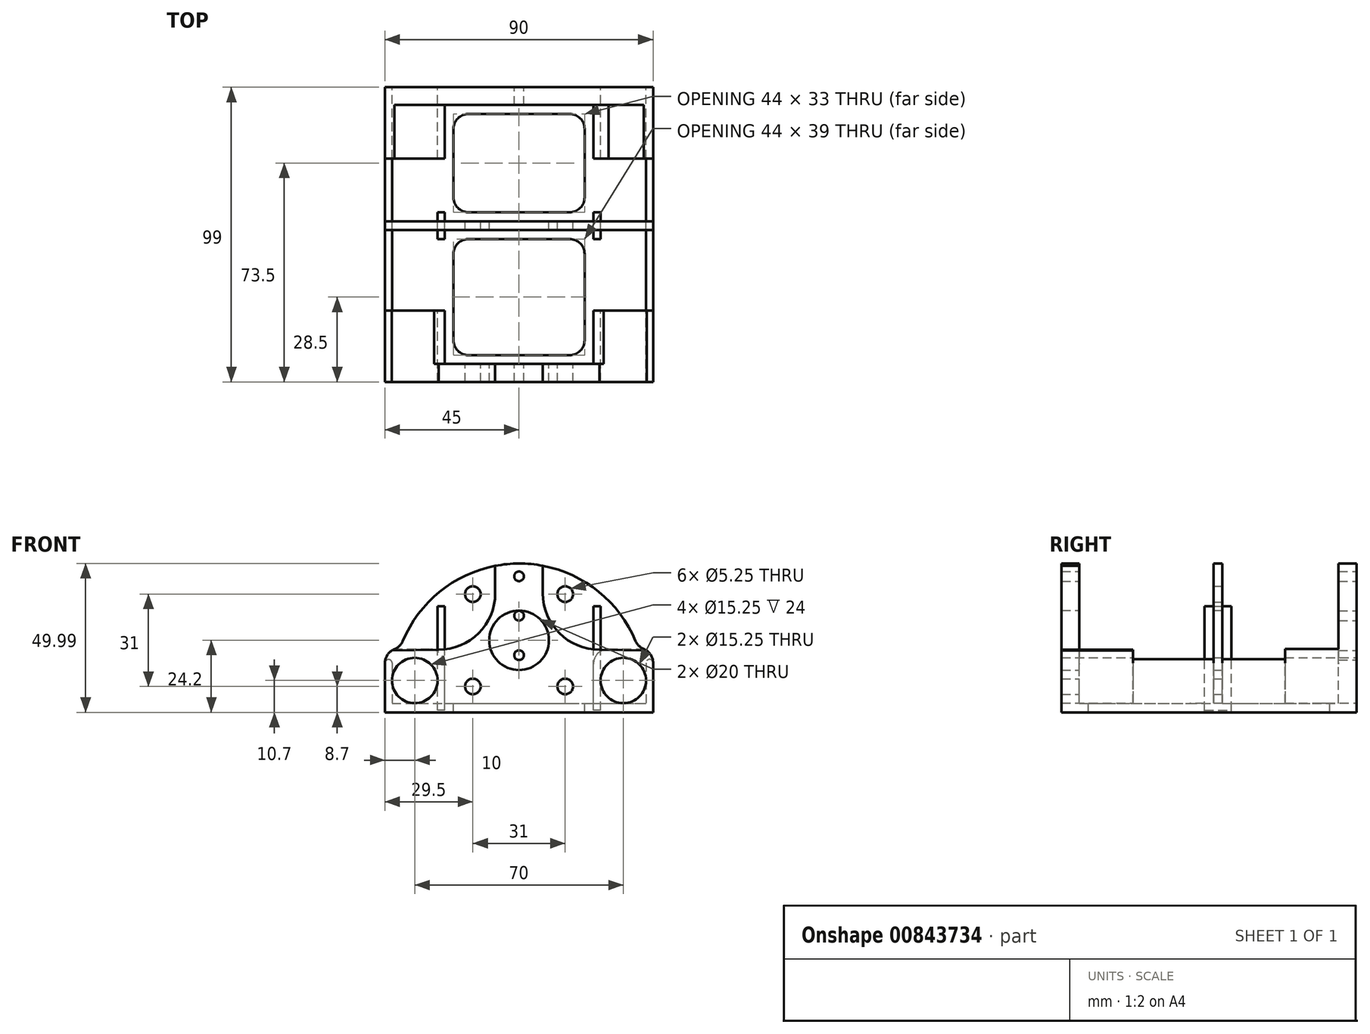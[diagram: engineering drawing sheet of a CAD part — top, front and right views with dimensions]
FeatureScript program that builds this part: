
annotation { "Feature Type Name" : "Feature", "Feature Type Description" : "" }
export const myFeature = defineFeature(function(context is Context, id is Id, definition is map)
    precondition{}
    {
        {
            var Q0;
            Q0=qCreatedBy(makeId("Front.planeOp"),FACE);
            var sketch = newSketch(context, id + "F0", { "sketchPlane" : qUnion([Q0])});
            skLineSegment(sketch, "E0", {"start": v(0, 0) * mm, "end": v(-52.92, 0) * mm, "construction": true});
            skLineSegment(sketch, "E1", {"start": v(-0.02, 0) * mm, "end": v(0, 0) * mm, "construction": true});
            skLineSegment(sketch, "E2", {"start": v(0, 0) * mm, "end": v(0, 49.26) * mm, "construction": true});
            skCircle(sketch, "E3", {"center": v(-35, 0) * mm, "radius": 7.62 * mm});
            skCircle(sketch, "E4", {"center": v(0, 8.5) * mm, "radius": 1.63 * mm});
            skCircle(sketch, "E5", {"center": v(0, 21.75) * mm, "radius": 1.63 * mm});
            skCircle(sketch, "E6", {"center": v(0, 35) * mm, "radius": 1.63 * mm});
            skLineSegment(sketch, "E7", {"start": v(45, 5.93) * mm, "end": v(45, -10) * mm});
            skLineSegment(sketch, "E8", {"start": v(45, -10) * mm, "end": v(-45, -10) * mm});
            skLineSegment(sketch, "E9", {"start": v(-45, -10) * mm, "end": v(-45, 5.86) * mm});
            skLineSegment(sketch, "E10", {"start": v(0, 0) * mm, "end": v(0, -24.97) * mm, "construction": true});
            skCircle(sketch, "E11", {"center": v(15.5, 29) * mm, "radius": 2.62 * mm});
            skCircle(sketch, "E12", {"center": v(-15.5, 29) * mm, "radius": 2.62 * mm});
            skCircle(sketch, "E13", {"center": v(15.5, -2) * mm, "radius": 2.62 * mm});
            skCircle(sketch, "E14", {"center": v(-15.5, -2) * mm, "radius": 2.62 * mm});
            skCircle(sketch, "E15", {"center": v(0, 13.5) * mm, "radius": 10 * mm});
            skLineSegment(sketch, "E16", {"start": v(25, 5.57) * mm, "end": v(25, -10) * mm});
            skLineSegment(sketch, "E17", {"start": v(-25, 5.52) * mm, "end": v(-25, -10) * mm});
            skCircle(sketch, "E18", {"center": v(35, 0) * mm, "radius": 7.62 * mm});
            skLineSegment(sketch, "E19", {"start": v(0, 0) * mm, "end": v(70, 0) * mm, "construction": true});
            skPoint(sketch, "E20.visualSharp", {"position": v(-45, 10) * mm});
            skArc(sketch, "E20.filletArc", {"start": v(-41.8, 10.52) * mm, "mid": v(-44.13, 8.68) * mm, "end": v(-45, 5.86) * mm});
            skArc(sketch, "E21.filletArc", {"start": v(-25, 5.52) * mm, "mid": v(-26.46, 9.06) * mm, "end": v(-30, 10.52) * mm});
            skArc(sketch, "E22.filletArc", {"start": v(30.06, 10.56) * mm, "mid": v(26.49, 9.12) * mm, "end": v(25, 5.57) * mm});
            skPoint(sketch, "E23.visualSharp", {"position": v(45, 10) * mm});
            skArc(sketch, "E23.filletArc", {"start": v(45, 5.93) * mm, "mid": v(44.14, 8.73) * mm, "end": v(41.87, 10.56) * mm});
            skLineSegment(sketch, "E24", {"start": v(42.62, -10) * mm, "end": v(42.62, 5.93) * mm});
            skArc(sketch, "E25", {"start": v(45, 5.93) * mm, "mid": v(43.81, 7.12) * mm, "end": v(42.62, 5.93) * mm});
            skLineSegment(sketch, "E26", {"start": v(-42.62, -10) * mm, "end": v(-42.62, 5.86) * mm});
            skArc(sketch, "E27", {"start": v(-42.62, 5.86) * mm, "mid": v(-43.81, 7.05) * mm, "end": v(-45, 5.86) * mm});
            skArc(sketch, "E28", {"start": v(39.13, 13.27) * mm, "mid": v(0.06, 39.29) * mm, "end": v(-39, 13.26) * mm});
            skPoint(sketch, "E29.visualSharp", {"position": v(-39.92, 10.86) * mm});
            skArc(sketch, "E29.filletArc", {"start": v(-41.8, 10.52) * mm, "mid": v(-40.13, 11.6) * mm, "end": v(-39, 13.26) * mm});
            skPoint(sketch, "E30.visualSharp", {"position": v(40.03, 10.93) * mm});
            skArc(sketch, "E30.filletArc", {"start": v(39.13, 13.27) * mm, "mid": v(40.23, 11.64) * mm, "end": v(41.87, 10.56) * mm});
            skLineSegment(sketch, "E31", {"start": v(-41.8, 10.52) * mm, "end": v(-30, 10.52) * mm});
            skLineSegment(sketch, "E32", {"start": v(41.87, 10.56) * mm, "end": v(30.06, 10.56) * mm});
            skLineSegment(sketch, "E33", {"start": v(22.5, -10) * mm, "end": v(22.5, 0) * mm});
            skLineSegment(sketch, "E34", {"start": v(27.38, -10) * mm, "end": v(27.38, 25) * mm});
            skLineSegment(sketch, "E35", {"start": v(25, 5.57) * mm, "end": v(25, 25) * mm});
            skLineSegment(sketch, "E36", {"start": v(25, 25) * mm, "end": v(27.38, 25) * mm});
            skLineSegment(sketch, "E37", {"start": v(-27.38, -10) * mm, "end": v(-27.38, 25) * mm});
            skLineSegment(sketch, "E38", {"start": v(-25, 5.52) * mm, "end": v(-25, 25) * mm});
            skLineSegment(sketch, "E39", {"start": v(-25, 25) * mm, "end": v(-27.38, 25) * mm});
            skSolve(sketch);
        }
        {
            var Q0;
            Q0=makeQuery(id+"F0.imprint","IMPRINT",FACE,{"disambiguationData":[TD([[makeQuery(id+"F0.imprint","IMPRINT",EDGE,{"derivedFrom":sQuery(id+"F0.wireOp",EDGE,"E6")}),-1.0]])]});
            var Q1;
            {var subQ4=sQuery(id+"F0.wireOp",EDGE,"E7");Q1=makeQuery(id+"F0.imprint","IMPRINT",FACE,{"disambiguationData":[TD([[makeQuery(id+"F0.imprint","IMPRINT",EDGE,{"derivedFrom":subQ4}),-1.0]])]});}
            var Q2;
            {var subQ6=sQuery(id+"F0.wireOp",EDGE,"ls8kvNI4-NHHg-Onv5-wAsb-4FJF5Vd8KV6a");Q2=makeQuery(id+"F0.imprint","IMPRINT",FACE,{"disambiguationData":[TD([[makeQuery(id+"F0.imprint","IMPRINT",EDGE,{"derivedFrom":subQ6}),-1.0]])]});}
            var Q3;
            {var subQ0=sQuery(id+"F0.wireOp",EDGE,"E17");Q3=makeQuery(id+"F0.imprint","IMPRINT",FACE,{"disambiguationData":[TD([[makeQuery(id+"F0.imprint","IMPRINT",EDGE,{"derivedFrom":subQ0}),-1.0]])]});}
            var Q4;
            {var subQ1=sQuery(id+"F0.wireOp",EDGE,"E9");Q4=makeQuery(id+"F0.imprint","IMPRINT",FACE,{"disambiguationData":[TD([[makeQuery(id+"F0.imprint","IMPRINT",EDGE,{"derivedFrom":subQ1}),-1.0]])]});}
            var Q5;
            Q5=makeQuery(id+"F0.imprint","IMPRINT",FACE,{"disambiguationData":[TD([[makeQuery(id+"F0.imprint","IMPRINT",EDGE,{"derivedFrom":sQuery(id+"F0.wireOp",EDGE,"E11")}),1.0]])]});
            var Q6;
            Q6=makeQuery(id+"F0.imprint","IMPRINT",FACE,{"disambiguationData":[TD([[makeQuery(id+"F0.imprint","IMPRINT",EDGE,{"derivedFrom":sQuery(id+"F0.wireOp",EDGE,"E12")}),1.0]])]});
            var Q7;
            Q7=makeQuery(id+"F0.imprint","IMPRINT",FACE,{"disambiguationData":[TD([[makeQuery(id+"F0.imprint","IMPRINT",EDGE,{"derivedFrom":sQuery(id+"F0.wireOp",EDGE,"E4")}),-1.0]])]});
            var Q8;
            Q8=makeQuery(id+"F0.imprint","IMPRINT",FACE,{"disambiguationData":[TD([[makeQuery(id+"F0.imprint","IMPRINT",EDGE,{"derivedFrom":sQuery(id+"F0.wireOp",EDGE,"E14")}),1.0]])]});
            var Q9;
            Q9=makeQuery(id+"F0.imprint","IMPRINT",FACE,{"disambiguationData":[TD([[makeQuery(id+"F0.imprint","IMPRINT",EDGE,{"derivedFrom":sQuery(id+"F0.wireOp",EDGE,"E13")}),1.0]])]});
            var Q10;
            {var subQ0=sQuery(id+"F0.wireOp",EDGE,"E16");Q10=makeQuery(id+"F0.imprint","IMPRINT",FACE,{"disambiguationData":[TD([[makeQuery(id+"F0.imprint","IMPRINT",EDGE,{"derivedFrom":subQ0}),1.0]])]});}
            var Q11;
            {var subQ1=sQuery(id+"F0.wireOp",EDGE,"E16");Q11=makeQuery(id+"F0.imprint","IMPRINT",FACE,{"disambiguationData":[TD([[makeQuery(id+"F0.imprint","IMPRINT",EDGE,{"derivedFrom":subQ1}),-1.0]])]});}
            var Q12;
            {var subQ1=sQuery(id+"F0.wireOp",EDGE,"E17");Q12=makeQuery(id+"F0.imprint","IMPRINT",FACE,{"disambiguationData":[TD([[makeQuery(id+"F0.imprint","IMPRINT",EDGE,{"derivedFrom":subQ1}),1.0]])]});}
            var Q13;
            {var subQ0=sQuery(id+"F0.wireOp",EDGE,"E35");Q13=makeQuery(id+"F0.imprint","IMPRINT",FACE,{"disambiguationData":[TD([[makeQuery(id+"F0.imprint","IMPRINT",EDGE,{"derivedFrom":subQ0}),-1.0]])]});}
            var Q14;
            {var subQ0=sQuery(id+"F0.wireOp",EDGE,"E38");Q14=makeQuery(id+"F0.imprint","IMPRINT",FACE,{"disambiguationData":[TD([[makeQuery(id+"F0.imprint","IMPRINT",EDGE,{"derivedFrom":subQ0}),1.0]])]});}
            var Q15;
            Q15=makeQuery(id+"F0.imprint","IMPRINT",FACE,{"disambiguationData":[TD([[makeQuery(id+"F0.imprint","IMPRINT",EDGE,{"derivedFrom":sQuery(id+"F0.wireOp",EDGE,"E23.filletArc")}),1.0]])]});
            var Q16;
            Q16=makeQuery(id+"F0.imprint","IMPRINT",FACE,{"disambiguationData":[TD([[makeQuery(id+"F0.imprint","IMPRINT",EDGE,{"derivedFrom":sQuery(id+"F0.wireOp",EDGE,"E20.filletArc")}),1.0]])]});
            var Q17;
            {var subQ0=sQuery(id+"F0.wireOp",EDGE,"E26");var subQ1=sQuery(id+"F0.wireOp",EDGE,"E3");var subQ2=makeQuery(id+"F0.imprint","INTERSECT",VERTEX,{"derivedFrom":[subQ1,subQ0]});Q17=makeQuery(id+"F0.imprint","IMPRINT",FACE,{"disambiguationData":[TD([[makeQuery(id+"F0.imprint","IMPRINT",EDGE,{"disambiguationData":[TD([[subQ2,-1.0]])],"derivedFrom":subQ1}),-1.0]])]});}
            var Q18;
            {var subQ0=sQuery(id+"F0.wireOp",EDGE,"E24");var subQ1=sQuery(id+"F0.wireOp",EDGE,"E8");var subQ2=makeQuery(id+"F0.imprint","INTERSECT",VERTEX,{"derivedFrom":[subQ1,subQ0]});Q18=makeQuery(id+"F0.imprint","IMPRINT",FACE,{"disambiguationData":[TD([[makeQuery(id+"F0.imprint","IMPRINT",EDGE,{"disambiguationData":[TD([[subQ2,-1.0]])],"derivedFrom":subQ1}),-1.0]])]});}
            extrude(context, id + "F1", {"entities" : qUnion([Q0, Q1, Q2, Q3, Q4, Q5, Q6, Q7, Q8, Q9, Q10, Q11, Q12, Q13, Q14, Q15, Q16, Q17, Q18]), "depth" : 6 * mm, "offsetDistance" : 25 * mm});
        }
        {
            var Q0;
            Q0=makeQuery(id+"F0.imprint","IMPRINT",FACE,{"disambiguationData":[TD([[makeQuery(id+"F0.imprint","IMPRINT",EDGE,{"derivedFrom":sQuery(id+"F0.wireOp",EDGE,"E6")}),-1.0]])]});
            var Q1;
            {var subQ0=sQuery(id+"F0.wireOp",EDGE,"E16");Q1=makeQuery(id+"F0.imprint","IMPRINT",FACE,{"disambiguationData":[TD([[makeQuery(id+"F0.imprint","IMPRINT",EDGE,{"derivedFrom":subQ0}),1.0]])]});}
            var Q2;
            {var subQ4=sQuery(id+"F0.wireOp",EDGE,"E7");Q2=makeQuery(id+"F0.imprint","IMPRINT",FACE,{"disambiguationData":[TD([[makeQuery(id+"F0.imprint","IMPRINT",EDGE,{"derivedFrom":subQ4}),-1.0]])]});}
            var Q3;
            {var subQ4=sQuery(id+"F0.wireOp",EDGE,"E9");Q3=makeQuery(id+"F0.imprint","IMPRINT",FACE,{"disambiguationData":[TD([[makeQuery(id+"F0.imprint","IMPRINT",EDGE,{"derivedFrom":subQ4}),-1.0]])]});}
            var Q4;
            Q4=makeQuery(id+"F0.imprint","IMPRINT",FACE,{"disambiguationData":[TD([[makeQuery(id+"F0.imprint","IMPRINT",EDGE,{"derivedFrom":sQuery(id+"F0.wireOp",EDGE,"E6")}),1.0]])]});
            var Q5;
            {var subQ1=sQuery(id+"F0.wireOp",EDGE,"E16");Q5=makeQuery(id+"F0.imprint","IMPRINT",FACE,{"disambiguationData":[TD([[makeQuery(id+"F0.imprint","IMPRINT",EDGE,{"derivedFrom":subQ1}),-1.0]])]});}
            var Q6;
            {var subQ1=sQuery(id+"F0.wireOp",EDGE,"E17");Q6=makeQuery(id+"F0.imprint","IMPRINT",FACE,{"disambiguationData":[TD([[makeQuery(id+"F0.imprint","IMPRINT",EDGE,{"derivedFrom":subQ1}),1.0]])]});}
            var Q7;
            Q7=makeQuery(id+"F0.imprint","IMPRINT",FACE,{"disambiguationData":[TD([[makeQuery(id+"F0.imprint","IMPRINT",EDGE,{"derivedFrom":sQuery(id+"F0.wireOp",EDGE,"E23.filletArc")}),1.0]])]});
            var Q8;
            {var subQ0=sQuery(id+"F0.wireOp",EDGE,"E24");var subQ1=sQuery(id+"F0.wireOp",EDGE,"E8");var subQ2=makeQuery(id+"F0.imprint","INTERSECT",VERTEX,{"derivedFrom":[subQ1,subQ0]});Q8=makeQuery(id+"F0.imprint","IMPRINT",FACE,{"disambiguationData":[TD([[makeQuery(id+"F0.imprint","IMPRINT",EDGE,{"disambiguationData":[TD([[subQ2,-1.0]])],"derivedFrom":subQ1}),-1.0]])]});}
            var Q9;
            Q9=makeQuery(id+"F0.imprint","IMPRINT",FACE,{"disambiguationData":[TD([[makeQuery(id+"F0.imprint","IMPRINT",EDGE,{"derivedFrom":sQuery(id+"F0.wireOp",EDGE,"E20.filletArc")}),1.0]])]});
            var Q10;
            {var subQ0=sQuery(id+"F0.wireOp",EDGE,"E35");Q10=makeQuery(id+"F0.imprint","IMPRINT",FACE,{"disambiguationData":[TD([[makeQuery(id+"F0.imprint","IMPRINT",EDGE,{"derivedFrom":subQ0}),-1.0]])]});}
            var Q11;
            {var subQ0=sQuery(id+"F0.wireOp",EDGE,"E38");Q11=makeQuery(id+"F0.imprint","IMPRINT",FACE,{"disambiguationData":[TD([[makeQuery(id+"F0.imprint","IMPRINT",EDGE,{"derivedFrom":subQ0}),1.0]])]});}
            var Q12;
            {var subQ1=sQuery(id+"F0.wireOp",EDGE,"E17");Q12=makeQuery(id+"F0.imprint","IMPRINT",FACE,{"disambiguationData":[TD([[makeQuery(id+"F0.imprint","IMPRINT",EDGE,{"derivedFrom":subQ1}),-1.0]])]});}
            var Q13;
            {var subQ0=sQuery(id+"F0.wireOp",EDGE,"E26");var subQ1=sQuery(id+"F0.wireOp",EDGE,"E3");var subQ2=makeQuery(id+"F0.imprint","INTERSECT",VERTEX,{"derivedFrom":[subQ1,subQ0]});Q13=makeQuery(id+"F0.imprint","IMPRINT",FACE,{"disambiguationData":[TD([[makeQuery(id+"F0.imprint","IMPRINT",EDGE,{"disambiguationData":[TD([[subQ2,-1.0]])],"derivedFrom":subQ1}),-1.0]])]});}
            extrude(context, id + "F2", {"entities" : qUnion([Q0, Q1, Q2, Q3, Q4, Q5, Q6, Q7, Q8, Q9, Q10, Q11, Q12, Q13]), "depth" : 48 * mm, "offsetDistance" : 25 * mm, "hasSecondDirection" : true, "secondDirectionOppositeDirection" : false, "secondDirectionDepth" : 45 * mm});
        }
        {
            var Q0;
            Q0 = qSketchRegion(id + "F0", true);
            var Q1;
            {var subQ0=sQuery(id+"F0.wireOp",EDGE,"E35");Q1=makeQuery(id+"F0.imprint","IMPRINT",FACE,{"disambiguationData":[TD([[makeQuery(id+"F0.imprint","IMPRINT",EDGE,{"derivedFrom":subQ0}),-1.0]])]});}
            var Q2;
            {var subQ0=sQuery(id+"F0.wireOp",EDGE,"E38");Q2=makeQuery(id+"F0.imprint","IMPRINT",FACE,{"disambiguationData":[TD([[makeQuery(id+"F0.imprint","IMPRINT",EDGE,{"derivedFrom":subQ0}),1.0]])]});}
            extrude(context, id + "F3", {"entities" : qUnion([Q0, Q1, Q2]), "depth" : 99 * mm, "offsetDistance" : 25 * mm, "hasSecondDirection" : true, "secondDirectionOppositeDirection" : false, "secondDirectionDepth" : 93 * mm});
        }
        {
            var Q0;
            Q0=makeQuery(id+"F0.imprint","IMPRINT",FACE,{"disambiguationData":[TD([[makeQuery(id+"F0.imprint","IMPRINT",EDGE,{"derivedFrom":sQuery(id+"F0.wireOp",EDGE,"E23.filletArc")}),1.0]])]});
            var Q1;
            {var subQ4=sQuery(id+"F0.wireOp",EDGE,"E16");Q1=makeQuery(id+"F0.imprint","IMPRINT",FACE,{"disambiguationData":[TD([[makeQuery(id+"F0.imprint","IMPRINT",EDGE,{"derivedFrom":subQ4}),1.0]])]});}
            var Q2;
            {var subQ0=sQuery(id+"F0.wireOp",EDGE,"E24");var subQ1=sQuery(id+"F0.wireOp",EDGE,"E8");var subQ2=makeQuery(id+"F0.imprint","INTERSECT",VERTEX,{"derivedFrom":[subQ1,subQ0]});Q2=makeQuery(id+"F0.imprint","IMPRINT",FACE,{"disambiguationData":[TD([[makeQuery(id+"F0.imprint","IMPRINT",EDGE,{"disambiguationData":[TD([[subQ2,-1.0]])],"derivedFrom":subQ1}),-1.0]])]});}
            var Q3;
            {var subQ4=sQuery(id+"F0.wireOp",EDGE,"E7");Q3=makeQuery(id+"F0.imprint","IMPRINT",FACE,{"disambiguationData":[TD([[makeQuery(id+"F0.imprint","IMPRINT",EDGE,{"derivedFrom":subQ4}),-1.0]])]});}
            var Q4;
            Q4=makeQuery(id+"F0.imprint","IMPRINT",FACE,{"disambiguationData":[TD([[makeQuery(id+"F0.imprint","IMPRINT",EDGE,{"derivedFrom":sQuery(id+"F0.wireOp",EDGE,"E20.filletArc")}),1.0]])]});
            var Q5;
            {var subQ0=sQuery(id+"F0.wireOp",EDGE,"E26");var subQ1=sQuery(id+"F0.wireOp",EDGE,"E3");var subQ2=makeQuery(id+"F0.imprint","INTERSECT",VERTEX,{"derivedFrom":[subQ1,subQ0]});Q5=makeQuery(id+"F0.imprint","IMPRINT",FACE,{"disambiguationData":[TD([[makeQuery(id+"F0.imprint","IMPRINT",EDGE,{"disambiguationData":[TD([[subQ2,-1.0]])],"derivedFrom":subQ1}),-1.0]])]});}
            var Q6;
            {var subQ3=sQuery(id+"F0.wireOp",EDGE,"E9");Q6=makeQuery(id+"F0.imprint","IMPRINT",FACE,{"disambiguationData":[TD([[makeQuery(id+"F0.imprint","IMPRINT",EDGE,{"derivedFrom":subQ3}),-1.0]])]});}
            var Q7;
            {var subQ1=sQuery(id+"F0.wireOp",EDGE,"E17");Q7=makeQuery(id+"F0.imprint","IMPRINT",FACE,{"disambiguationData":[TD([[makeQuery(id+"F0.imprint","IMPRINT",EDGE,{"derivedFrom":subQ1}),-1.0]])]});}
            extrude(context, id + "F4", {"entities" : qUnion([Q0, Q1, Q2, Q3, Q4, Q5, Q6, Q7]), "operationType" : NewBodyOperationType.ADD, "depth" : 24 * mm, "offsetDistance" : 25 * mm});
        }
        {
            var Q0;
            Q0=makeQuery(id+"F0.imprint","IMPRINT",FACE,{"disambiguationData":[TD([[makeQuery(id+"F0.imprint","IMPRINT",EDGE,{"derivedFrom":sQuery(id+"F0.wireOp",EDGE,"ls8kvNI4-NHHg-Onv5-wAsb-4FJF5Vd8KV6a")}),-1.0]])]});
            var Q1;
            {var subQ0=sQuery(id+"F0.wireOp",EDGE,"E16");Q1=makeQuery(id+"F0.imprint","IMPRINT",FACE,{"disambiguationData":[TD([[makeQuery(id+"F0.imprint","IMPRINT",EDGE,{"derivedFrom":subQ0}),1.0]])]});}
            var Q2;
            {var subQ4=sQuery(id+"F0.wireOp",EDGE,"E7");Q2=makeQuery(id+"F0.imprint","IMPRINT",FACE,{"disambiguationData":[TD([[makeQuery(id+"F0.imprint","IMPRINT",EDGE,{"derivedFrom":subQ4}),-1.0]])]});}
            var Q3;
            {var subQ4=sQuery(id+"F0.wireOp",EDGE,"E9");Q3=makeQuery(id+"F0.imprint","IMPRINT",FACE,{"disambiguationData":[TD([[makeQuery(id+"F0.imprint","IMPRINT",EDGE,{"derivedFrom":subQ4}),-1.0]])]});}
            var Q4;
            Q4=makeQuery(id+"F0.imprint","IMPRINT",FACE,{"disambiguationData":[TD([[makeQuery(id+"F0.imprint","IMPRINT",EDGE,{"derivedFrom":sQuery(id+"F0.wireOp",EDGE,"E23.filletArc")}),1.0]])]});
            var Q5;
            {var subQ0=sQuery(id+"F0.wireOp",EDGE,"E24");var subQ1=sQuery(id+"F0.wireOp",EDGE,"E8");var subQ2=makeQuery(id+"F0.imprint","INTERSECT",VERTEX,{"derivedFrom":[subQ1,subQ0]});Q5=makeQuery(id+"F0.imprint","IMPRINT",FACE,{"disambiguationData":[TD([[makeQuery(id+"F0.imprint","IMPRINT",EDGE,{"disambiguationData":[TD([[subQ2,-1.0]])],"derivedFrom":subQ1}),-1.0]])]});}
            var Q6;
            Q6=makeQuery(id+"F0.imprint","IMPRINT",FACE,{"disambiguationData":[TD([[makeQuery(id+"F0.imprint","IMPRINT",EDGE,{"derivedFrom":sQuery(id+"F0.wireOp",EDGE,"E20.filletArc")}),1.0]])]});
            var Q7;
            {var subQ1=sQuery(id+"F0.wireOp",EDGE,"E17");Q7=makeQuery(id+"F0.imprint","IMPRINT",FACE,{"disambiguationData":[TD([[makeQuery(id+"F0.imprint","IMPRINT",EDGE,{"derivedFrom":subQ1}),-1.0]])]});}
            var Q8;
            {var subQ0=sQuery(id+"F0.wireOp",EDGE,"E26");var subQ1=sQuery(id+"F0.wireOp",EDGE,"E3");var subQ2=makeQuery(id+"F0.imprint","INTERSECT",VERTEX,{"derivedFrom":[subQ1,subQ0]});Q8=makeQuery(id+"F0.imprint","IMPRINT",FACE,{"disambiguationData":[TD([[makeQuery(id+"F0.imprint","IMPRINT",EDGE,{"disambiguationData":[TD([[subQ2,-1.0]])],"derivedFrom":subQ1}),-1.0]])]});}
            extrude(context, id + "F5", {"entities" : qUnion([Q0, Q1, Q2, Q3, Q4, Q5, Q6, Q7, Q8]), "operationType" : NewBodyOperationType.ADD, "depth" : 99 * mm, "offsetDistance" : 25 * mm, "hasSecondDirection" : true, "secondDirectionOppositeDirection" : false, "secondDirectionDepth" : 75 * mm});
        }
        {
            var Q0;
            Q0=makeQuery(id+"F0.imprint","IMPRINT",FACE,{"disambiguationData":[TD([[makeQuery(id+"F0.imprint","IMPRINT",EDGE,{"derivedFrom":sQuery(id+"F0.wireOp",EDGE,"E6")}),-1.0]])]});
            var sketch = newSketch(context, id + "F6", { "sketchPlane" : qUnion([Q0])});
            skLineSegment(sketch, "E40.bottom", {"start": v(45, -10.7) * mm, "end": v(-45, -10.7) * mm});
            skLineSegment(sketch, "E40.top", {"start": v(45, -7.7) * mm, "end": v(-45, -7.7) * mm});
            skLineSegment(sketch, "E40.left", {"start": v(45, -10.7) * mm, "end": v(45, -7.7) * mm});
            skLineSegment(sketch, "E40.right", {"start": v(-45, -10.7) * mm, "end": v(-45, -7.7) * mm});
            skLineSegment(sketch, "E41", {"start": v(0, 0) * mm, "end": v(0, -26.9) * mm, "construction": true});
            skSolve(sketch);
        }
        {
            var Q0;
            Q0 = qSketchRegion(id + "F6", true);
            extrude(context, id + "F7", {"entities" : qUnion([Q0]), "depth" : 99 * mm, "offsetDistance" : 25 * mm});
        }
        {
            var Q0;
            Q0=makeQuery(id+"F7.opExtrude","SWEPT_FACE",FACE,{"disambiguationData":[OSD([sQuery(id+"F6.wireOp",EDGE,"E40.top")])]});
            var sketch = newSketch(context, id + "F8", { "sketchPlane" : qUnion([Q0])});
            skLineSegment(sketch, "E42.bottom", {"start": v(-17, -90) * mm, "end": v(17, -90) * mm});
            skLineSegment(sketch, "E42.top", {"start": v(-17, -51) * mm, "end": v(17, -51) * mm});
            skLineSegment(sketch, "E42.left", {"start": v(-22, -85) * mm, "end": v(-22, -56) * mm});
            skLineSegment(sketch, "E42.right", {"start": v(22, -85) * mm, "end": v(22, -56) * mm});
            skLineSegment(sketch, "E43.bottom", {"start": v(-17, -42) * mm, "end": v(17, -42) * mm});
            skLineSegment(sketch, "E43.top", {"start": v(-17, -9) * mm, "end": v(17, -9) * mm});
            skLineSegment(sketch, "E43.left", {"start": v(-22, -37) * mm, "end": v(-22, -14) * mm});
            skLineSegment(sketch, "E43.right", {"start": v(22, -37) * mm, "end": v(22, -14) * mm});
            skLineSegment(sketch, "E44", {"start": v(0, 0) * mm, "end": v(0, -96.08) * mm, "construction": true});
            skPoint(sketch, "E45.visualSharp", {"position": v(22, -9) * mm});
            skArc(sketch, "E45.filletArc", {"start": v(22, -14) * mm, "mid": v(20.54, -10.46) * mm, "end": v(17, -9) * mm});
            skPoint(sketch, "E46.visualSharp", {"position": v(22, -42) * mm});
            skArc(sketch, "E46.filletArc", {"start": v(17, -42) * mm, "mid": v(20.54, -40.54) * mm, "end": v(22, -37) * mm});
            skPoint(sketch, "E47.visualSharp", {"position": v(22, -51) * mm});
            skArc(sketch, "E47.filletArc", {"start": v(22, -56) * mm, "mid": v(20.54, -52.46) * mm, "end": v(17, -51) * mm});
            skPoint(sketch, "E48.visualSharp", {"position": v(22, -90) * mm});
            skArc(sketch, "E48.filletArc", {"start": v(17, -90) * mm, "mid": v(20.54, -88.54) * mm, "end": v(22, -85) * mm});
            skPoint(sketch, "E49.visualSharp", {"position": v(-22, -90) * mm});
            skArc(sketch, "E49.filletArc", {"start": v(-22, -85) * mm, "mid": v(-20.54, -88.54) * mm, "end": v(-17, -90) * mm});
            skPoint(sketch, "E50.visualSharp", {"position": v(-22, -51) * mm});
            skArc(sketch, "E50.filletArc", {"start": v(-17, -51) * mm, "mid": v(-20.54, -52.46) * mm, "end": v(-22, -56) * mm});
            skPoint(sketch, "E51.visualSharp", {"position": v(-22, -42) * mm});
            skArc(sketch, "E51.filletArc", {"start": v(-22, -37) * mm, "mid": v(-20.54, -40.54) * mm, "end": v(-17, -42) * mm});
            skPoint(sketch, "E52.visualSharp", {"position": v(-22, -9) * mm});
            skArc(sketch, "E52.filletArc", {"start": v(-17, -9) * mm, "mid": v(-20.54, -10.46) * mm, "end": v(-22, -14) * mm});
            skSolve(sketch);
        }
        {
            var Q0;
            Q0=makeQuery(id+"F8.imprint","IMPRINT",FACE,{"disambiguationData":[TD([[makeQuery(id+"F8.imprint","IMPRINT",EDGE,{"derivedFrom":sQuery(id+"F8.wireOp",EDGE,"E42.bottom")}),1.0]])]});
            var Q1;
            Q1=makeQuery(id+"F8.imprint","IMPRINT",FACE,{"disambiguationData":[TD([[makeQuery(id+"F8.imprint","IMPRINT",EDGE,{"derivedFrom":sQuery(id+"F8.wireOp",EDGE,"E43.bottom")}),1.0]])]});
            extrude(context, id + "F9", {"entities" : qUnion([Q0, Q1]), "operationType" : NewBodyOperationType.REMOVE, "oppositeDirection" : true, "depth" : 25 * mm, "offsetDistance" : 25 * mm});
        }
        {
            var Q0;
            {var subQ4=sQuery(id+"F0.wireOp",EDGE,"E7");Q0=makeQuery(id+"F0.imprint","IMPRINT",FACE,{"disambiguationData":[TD([[makeQuery(id+"F0.imprint","IMPRINT",EDGE,{"derivedFrom":subQ4}),-1.0]])]});}
            var Q1;
            {var subQ4=sQuery(id+"F0.wireOp",EDGE,"E9");Q1=makeQuery(id+"F0.imprint","IMPRINT",FACE,{"disambiguationData":[TD([[makeQuery(id+"F0.imprint","IMPRINT",EDGE,{"derivedFrom":subQ4}),-1.0]])]});}
            extrude(context, id + "F10", {"entities" : qUnion([Q0, Q1]), "operationType" : NewBodyOperationType.ADD, "depth" : 93 * mm, "offsetDistance" : 25 * mm});
        }
        {
            var Q0;
            Q0=makeQuery(id+"F3.opExtrude","CAP_FACE",FACE,{"disambiguationData":[OSD([sQuery(id+"F0.wireOp",EDGE,"E3"),sQuery(id+"F0.wireOp",EDGE,"E4"),sQuery(id+"F0.wireOp",EDGE,"E5"),sQuery(id+"F0.wireOp",EDGE,"E6"),sQuery(id+"F0.wireOp",EDGE,"E7"),sQuery(id+"F0.wireOp",EDGE,"E8"),sQuery(id+"F0.wireOp",EDGE,"E9"),sQuery(id+"F0.wireOp",EDGE,"xWTqpVJG-LeZE-ckjX-DmdP-jzXZU0kw2qfi"),sQuery(id+"F0.wireOp",EDGE,"E18")])],"isStart":false});
            var sketch = newSketch(context, id + "F11", { "sketchPlane" : qUnion([Q0])});
            skArc(sketch, "E53", {"start": v(-27, 10.32) * mm, "mid": v(-13.56, 15.89) * mm, "end": v(-8, 29.32) * mm});
            skArc(sketch, "E54", {"start": v(8, 29.32) * mm, "mid": v(13.56, 15.89) * mm, "end": v(27, 10.32) * mm});
            skLineSegment(sketch, "E55", {"start": v(-55.07, 10.32) * mm, "end": v(54.12, 10.32) * mm, "construction": true});
            skLineSegment(sketch, "E56", {"start": v(8, -23.39) * mm, "end": v(8, 55.23) * mm, "construction": true});
            skLineSegment(sketch, "E57", {"start": v(-8, -19.64) * mm, "end": v(-8, 59.13) * mm, "construction": true});
            skLineSegment(sketch, "E58", {"start": v(-27, 10.32) * mm, "end": v(-45, 10) * mm});
            skLineSegment(sketch, "E59", {"start": v(27, 10.32) * mm, "end": v(45, 10) * mm});
            skLineSegment(sketch, "E60", {"start": v(8, 29.32) * mm, "end": v(8, 38.6) * mm});
            skLineSegment(sketch, "E61", {"start": v(-8, 29.32) * mm, "end": v(-8, 38.6) * mm});
            skLineSegment(sketch, "E62", {"start": v(-8, 29.32) * mm, "end": v(-8, -10) * mm});
            skLineSegment(sketch, "E63", {"start": v(8, 29.32) * mm, "end": v(8, -10) * mm});
            skLineSegment(sketch, "E64", {"start": v(8, 29.32) * mm, "end": v(8, 38.6) * mm, "construction": true});
            skLineSegment(sketch, "E65", {"start": v(-8, 29.32) * mm, "end": v(-8, 38.6) * mm, "construction": true});
            skSolve(sketch);
        }
        {
            var Q0;
            {var subQ0=sQuery(id+"F11.wireOp",EDGE,"E53");var subQ1=makeQuery(id+"F3.opExtrude","CAP_EDGE",EDGE,{"disambiguationData":[OSD([sQuery(id+"F0.wireOp",EDGE,"xWTqpVJG-LeZE-ckjX-DmdP-jzXZU0kw2qfi")])],"isStart":false});var subQ3=makeQuery(id+"F11.imprint","INTERSECT",VERTEX,{"derivedFrom":[subQ1,subQ0]});Q0=makeQuery(id+"F11.imprint","IMPRINT",FACE,{"disambiguationData":[TD([[makeQuery(id+"F11.imprint","IMPRINT",EDGE,{"disambiguationData":[TD([[subQ3,1.0]])],"derivedFrom":subQ0}),1.0]])]});}
            var Q1;
            {var subQ0=sQuery(id+"F11.wireOp",EDGE,"E54");var subQ1=makeQuery(id+"F3.opExtrude","CAP_EDGE",EDGE,{"disambiguationData":[OSD([sQuery(id+"F0.wireOp",EDGE,"xWTqpVJG-LeZE-ckjX-DmdP-jzXZU0kw2qfi")])],"isStart":false});var subQ3=makeQuery(id+"F11.imprint","INTERSECT",VERTEX,{"derivedFrom":[subQ1,subQ0]});Q1=makeQuery(id+"F11.imprint","IMPRINT",FACE,{"disambiguationData":[TD([[makeQuery(id+"F11.imprint","IMPRINT",EDGE,{"disambiguationData":[TD([[subQ3,-1.0]])],"derivedFrom":subQ0}),1.0]])]});}
            extrude(context, id + "F12", {"entities" : qUnion([Q0, Q1]), "operationType" : NewBodyOperationType.REMOVE, "oppositeDirection" : true, "depth" : 25 * mm, "offsetDistance" : 25 * mm});
        }
        {
            var Q0;
            {var subQ0=sQuery(id+"F0.wireOp",EDGE,"E35");Q0=makeQuery(id+"F0.imprint","IMPRINT",FACE,{"disambiguationData":[TD([[makeQuery(id+"F0.imprint","IMPRINT",EDGE,{"derivedFrom":subQ0}),-1.0]])]});}
            var Q1;
            {var subQ0=sQuery(id+"F0.wireOp",EDGE,"E38");Q1=makeQuery(id+"F0.imprint","IMPRINT",FACE,{"disambiguationData":[TD([[makeQuery(id+"F0.imprint","IMPRINT",EDGE,{"derivedFrom":subQ0}),1.0]])]});}
            var Q2;
            {var subQ4=sQuery(id+"F0.wireOp",EDGE,"E16");Q2=makeQuery(id+"F0.imprint","IMPRINT",FACE,{"disambiguationData":[TD([[makeQuery(id+"F0.imprint","IMPRINT",EDGE,{"derivedFrom":subQ4}),1.0]])]});}
            var Q3;
            {var subQ1=sQuery(id+"F0.wireOp",EDGE,"E17");Q3=makeQuery(id+"F0.imprint","IMPRINT",FACE,{"disambiguationData":[TD([[makeQuery(id+"F0.imprint","IMPRINT",EDGE,{"derivedFrom":subQ1}),-1.0]])]});}
            extrude(context, id + "F13", {"entities" : qUnion([Q0, Q1, Q2, Q3]), "depth" : 51 * mm, "offsetDistance" : 25 * mm, "hasSecondDirection" : true, "secondDirectionOppositeDirection" : false, "secondDirectionDepth" : 42 * mm});
        }
    });
